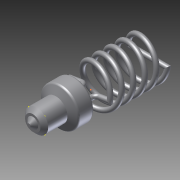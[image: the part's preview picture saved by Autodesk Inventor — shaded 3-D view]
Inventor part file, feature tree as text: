
AUTODESK INVENTOR PART (.ipt)
format: ipt  version: 2011 SP2 (Build 150309200, 309)  size: 438,784 bytes
history: native  units: mm
features: sketch x5, plane x2, other x2, revolve x1, fillet x1, chamfer x1, sweep x1
ambient origin geometry x8: Origin, YZ Plane, XZ Plane, XY Plane, X Axis, Y Axis, Z Axis, Center Point
bodies: Solid1 (feature_tree)
feature tree (13):
  revolve  "Revolution1"  [1 undecoded]
  fillet  "Fillet1"  Radius=20.0mm
  chamfer  "Chamfer1"  Distance=15.0mm
  plane  "Work Plane1"
  sketch  "Sketch2"  dims[d3=30.0mm]
  sweep  "Sweep1"
  plane  "Work Plane2"
  sketch  "Sketch4"  dims[d5=45.0deg d6=15.0mm d7=5.0mm d8=90.0deg d9=3.0mm d10=5.0mm d11=2.0mm d12=45.0deg d13=20.0mm d14=30.0mm d15=25.0mm d16=50.0mm d17=0.0mm d18=30.0mm d19=25.0mm d20=50.0mm d21=0.0mm d28=7.0mm d29=7.0mm d30=20.0mm d31=20.0mm d32=6.0mm d33=6.0mm d34=3.0mm d35=0.0mm d36=-5.0mm]
  sketch  "Sketch1"  dims[d0=60.0mm d1=25.0mm d2=20.0mm]
  sketch  "3D Sketch1"
  other  "Helical Curve1"
  other  "Helical Curve2"
  sketch  "Sketch3"  dims[d4=2.0mm]
note: 1 required parameter value undecoded (feature->parameter linkage not recoverable at this tier; creation-order binding heuristic only, values carry confidence <= 0.55)
